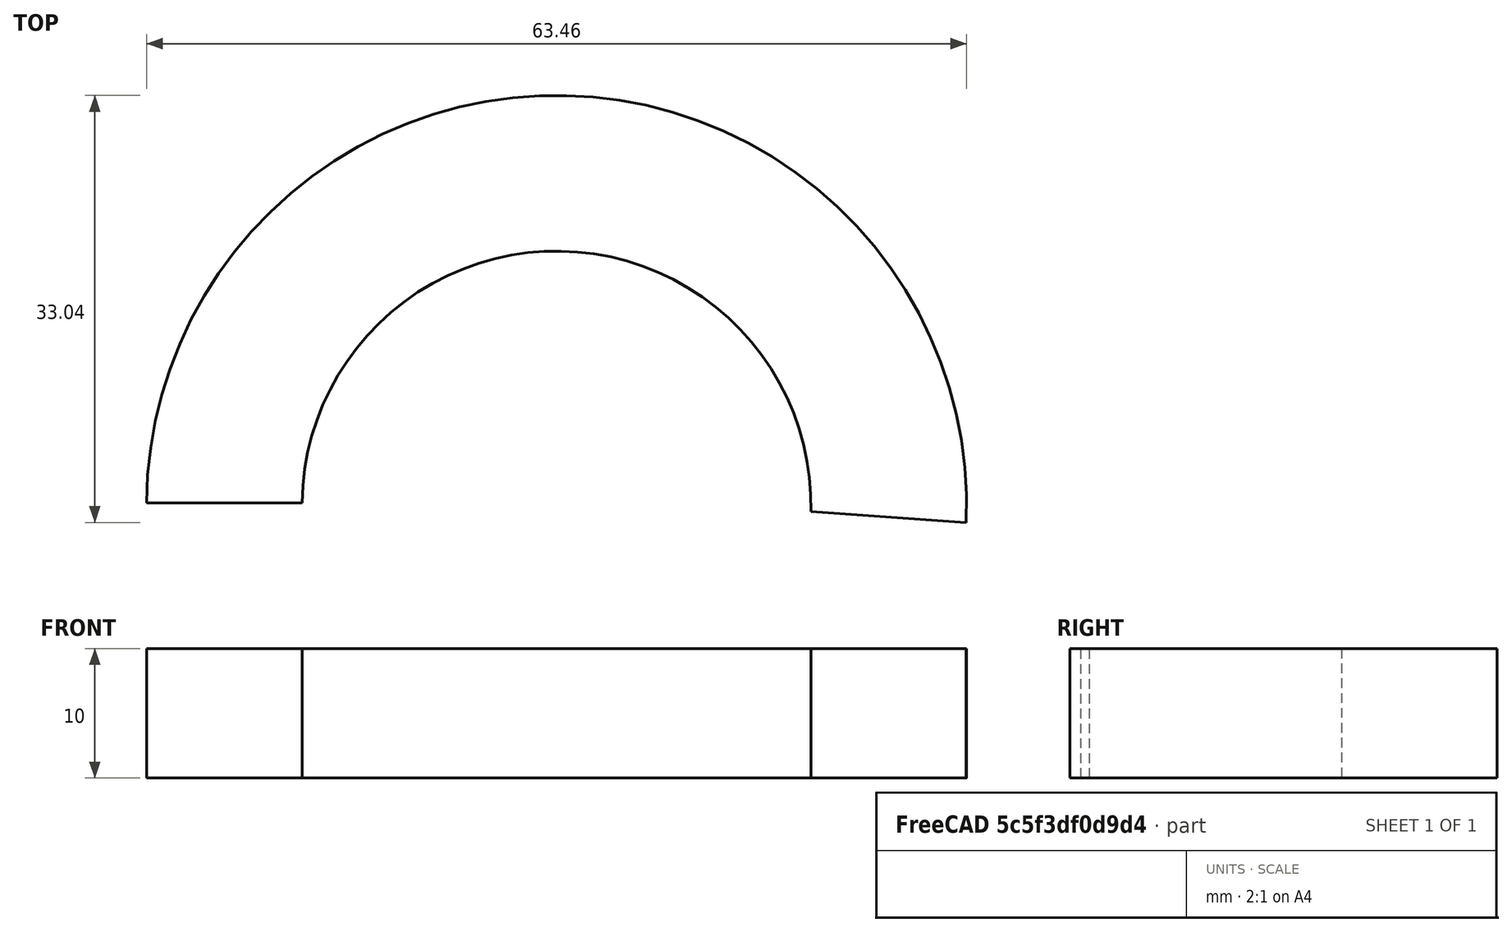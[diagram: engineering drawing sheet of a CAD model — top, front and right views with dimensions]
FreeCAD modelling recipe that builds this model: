
FCSTD DOCUMENT  (FreeCAD 1.0R39109 (Git))
Label: latch02
License: All rights reserved
LicenseURL: https://en.wikipedia.org/wiki/All_rights_reserved
objects: PartDesign::Body×2, Sketcher::SketchObject×1, PartDesign::Pad×1, App::Part×1
note: 7 computed .brp shape members not serialized (recipe doc carries the construction recipe); baked Part::Feature solids carry a one-line shape summary decoded from their .brp

FEATURE [Sketcher::SketchObject] Sketch
  ArcFitTolerance = 1e-06
  AttachmentSupport = -> [XY_Plane001]
  FullyConstrained = false
  MakeInternals = false
  MapMode = 5
  sketch-geometry (4):
    g0: ArcOfCircle CenterX=0 CenterY=31.4481 CenterZ=0 NormalX=0 NormalY=0 NormalZ=1 AngleXU=0 Radius=19.6884 StartAngle=6.2602 EndAngle=9.41354
    g1: ArcOfCircle CenterX=0 CenterY=31.4481 CenterZ=0 NormalX=0 NormalY=0 NormalZ=1 AngleXU=0 Radius=31.7291 StartAngle=6.2421 EndAngle=9.41781
    g2: LineSegment StartX=-31.7283 StartY=31.6693 StartZ=0 EndX=-19.6872 EndY=31.6693 EndZ=0
    g3: LineSegment StartX=19.6832 StartY=30.9956 StartZ=0 EndX=31.7023 EndY=30.145 EndZ=0
  constraints (7):
    c: PointOnObject(g0,g-2)
    c: Coincident(g1,g0)
    c: Coincident(g2,g1)
    c: Coincident(g2,g0)
    c: Horizontal(g2)
    c: Coincident(g3,g0)
    c: Coincident(g3,g1)
FEATURE [PartDesign::Pad] Pad
  Direction = (0,0,1)
  Length = 10
  Length2 = 10
  Profile = -> Sketch
  ReferenceAxis = -> Sketch [N_Axis]
  Refine = true
  Suppressed = false
  Type = 0
FEATURE [PartDesign::Body] Body
  AllowCompound = false
  Group = -> [Sketch,Pad]
  Origin = -> Origin001
  Tip = -> Pad
FEATURE [PartDesign::Body] Body001
  AllowCompound = false
  Origin = -> Origin002
FEATURE [App::Part] Part
  Group = -> [Body,Body001]
  Origin = -> Origin
